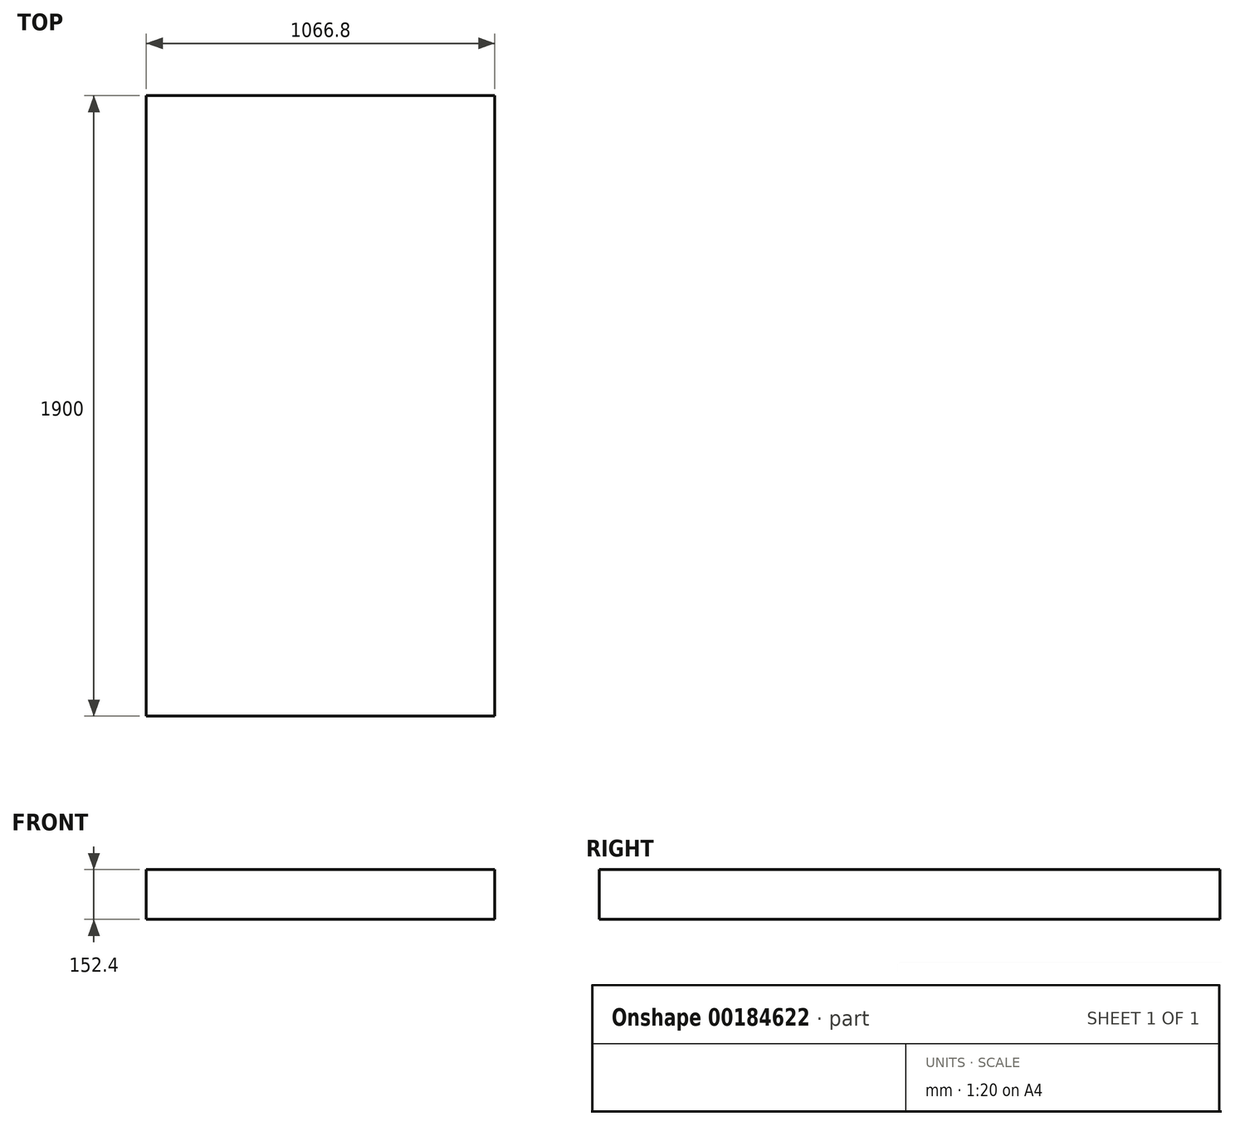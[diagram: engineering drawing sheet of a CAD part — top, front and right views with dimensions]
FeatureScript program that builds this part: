
annotation { "Feature Type Name" : "Feature", "Feature Type Description" : "" }
export const myFeature = defineFeature(function(context is Context, id is Id, definition is map)
    precondition{}
    {
        {
            var Q0;
            Q0=qCreatedBy(makeId("Front.planeOp"),FACE);
            var sketch = newSketch(context, id + "F0", { "sketchPlane" : qUnion([Q0])});
            skLineSegment(sketch, "E0.bottom", {"start": v(533.4, -76.2) * mm, "end": v(-533.4, -76.2) * mm});
            skLineSegment(sketch, "E0.top", {"start": v(533.4, 76.2) * mm, "end": v(-533.4, 76.2) * mm});
            skLineSegment(sketch, "E0.left", {"start": v(533.4, -76.2) * mm, "end": v(533.4, 76.2) * mm});
            skLineSegment(sketch, "E0.right", {"start": v(-533.4, -76.2) * mm, "end": v(-533.4, 76.2) * mm});
            skPoint(sketch, "E0.middle", {"position": v(0, 0) * mm});
            skSolve(sketch);
        }
        {
            var Q0;
            Q0 = qSketchRegion(id + "F0", true);
            extrude(context, id + "F1", {"entities" : qUnion([Q0]), "endBound" : BoundingType.SYMMETRIC, "depth" : 1900 * mm});
        }
    });
